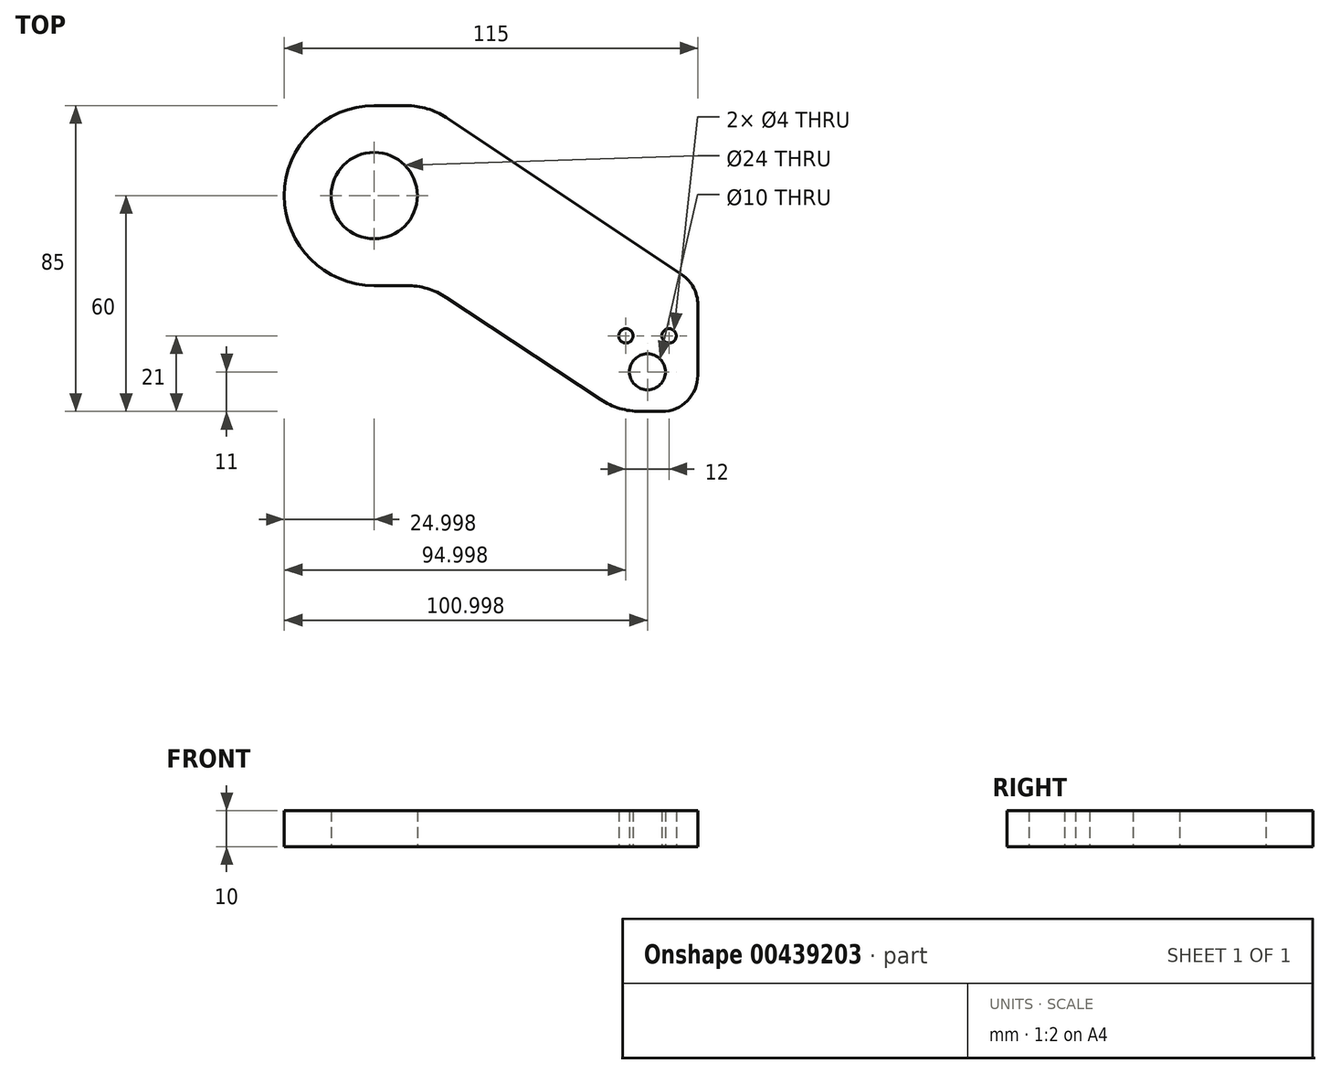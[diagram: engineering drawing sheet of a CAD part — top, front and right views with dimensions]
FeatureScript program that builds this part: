
annotation { "Feature Type Name" : "Feature", "Feature Type Description" : "" }
export const myFeature = defineFeature(function(context is Context, id is Id, definition is map)
    precondition{}
    {
        {
            var Q0;
            Q0=qCreatedBy(makeId("Top.planeOp"),FACE);
            var sketch = newSketch(context, id + "F0", { "sketchPlane" : qUnion([Q0])});
            skLineSegment(sketch, "E0", {"start": v(-66.96, 50) * mm, "end": v(-66.96, 0) * mm});
            skLineSegment(sketch, "E1", {"start": v(-26.96, 0) * mm, "end": v(-66.96, 0) * mm});
            skLineSegment(sketch, "E2", {"start": v(-26.96, 0) * mm, "end": v(26.04, -35) * mm});
            skLineSegment(sketch, "E3", {"start": v(48.04, -35) * mm, "end": v(26.04, -35) * mm});
            skLineSegment(sketch, "E4", {"start": v(48.04, 0) * mm, "end": v(48.04, -35) * mm});
            skLineSegment(sketch, "E5", {"start": v(-66.96, 50) * mm, "end": v(-26.96, 50) * mm});
            skCircle(sketch, "E6", {"center": v(-41.96, 25) * mm, "radius": 12 * mm});
            skCircle(sketch, "E7", {"center": v(34.04, -24) * mm, "radius": 5 * mm});
            skLineSegment(sketch, "E8", {"start": v(-26.96, 50) * mm, "end": v(48.04, 0) * mm});
            skPoint(sketch, "E9.orphan", {"position": v(48.04, 50) * mm});
            skCircle(sketch, "E10", {"center": v(40.04, -14) * mm, "radius": 2 * mm});
            skLineSegment(sketch, "E11", {"start": v(34.04, 49.72) * mm, "end": v(34.04, -39.59) * mm, "construction": true});
            skCircle(sketch, "E12.MirrorC", {"center": v(28.04, -14) * mm, "radius": 2 * mm});
            skSolve(sketch);
        }
        {
            var Q0;
            Q0 = qSketchRegion(id + "F0", true);
            extrude(context, id + "F1", {"entities" : qUnion([Q0]), "depth" : 10 * mm});
        }
        {
            var Q0;
            Q0=makeQuery(id+"F1.opExtrude","SWEPT_EDGE",EDGE,{"disambiguationData":[OSD([sQuery(id+"F0.wireOp",EDGE,"E0"),sQuery(id+"F0.wireOp",EDGE,"E5")])]});
            var Q1;
            Q1=makeQuery(id+"F1.opExtrude","SWEPT_EDGE",EDGE,{"disambiguationData":[OSD([sQuery(id+"F0.wireOp",EDGE,"E0"),sQuery(id+"F0.wireOp",EDGE,"E1")])]});
            fillet(context, id + "F2", {"entities" : qUnion([Q0, Q1]), "radius" : 25 * mm, "tangentPropagation" : true, "allowEdgeOverflow" : false});
        }
        {
            var Q0;
            Q0=makeQuery(id+"F1.opExtrude","SWEPT_EDGE",EDGE,{"disambiguationData":[OSD([sQuery(id+"F0.wireOp",EDGE,"E3"),sQuery(id+"F0.wireOp",EDGE,"E4")])]});
            var Q1;
            Q1=makeQuery(id+"F1.opExtrude","SWEPT_EDGE",EDGE,{"disambiguationData":[OSD([sQuery(id+"F0.wireOp",EDGE,"E4"),sQuery(id+"F0.wireOp",EDGE,"E8")])]});
            fillet(context, id + "F3", {"entities" : qUnion([Q0, Q1]), "radius" : 10 * mm, "tangentPropagation" : true, "allowEdgeOverflow" : false});
        }
        {
            var Q0;
            Q0=makeQuery(id+"F1.opExtrude","SWEPT_EDGE",EDGE,{"disambiguationData":[OSD([sQuery(id+"F0.wireOp",EDGE,"E5"),sQuery(id+"F0.wireOp",EDGE,"E8")])]});
            var Q1;
            Q1=makeQuery(id+"F1.opExtrude","SWEPT_EDGE",EDGE,{"disambiguationData":[OSD([sQuery(id+"F0.wireOp",EDGE,"E1"),sQuery(id+"F0.wireOp",EDGE,"E2")])]});
            var Q2;
            Q2=makeQuery(id+"F1.opExtrude","SWEPT_EDGE",EDGE,{"disambiguationData":[OSD([sQuery(id+"F0.wireOp",EDGE,"E2"),sQuery(id+"F0.wireOp",EDGE,"E3")])]});
            fillet(context, id + "F4", {"entities" : qUnion([Q0, Q1, Q2]), "radius" : 20 * mm, "tangentPropagation" : true, "allowEdgeOverflow" : false});
        }
    });
